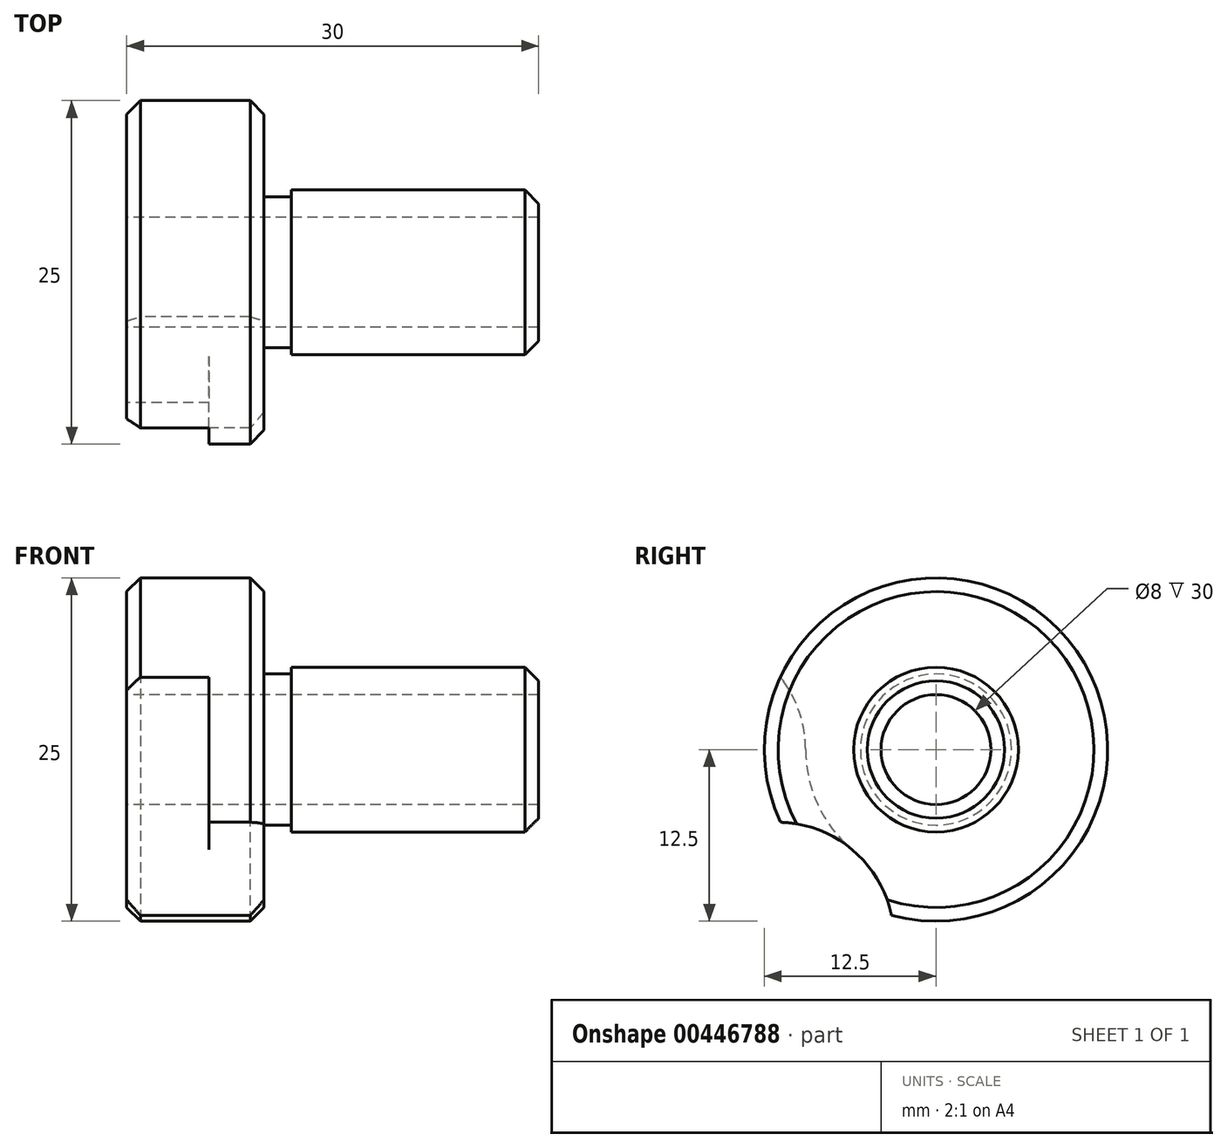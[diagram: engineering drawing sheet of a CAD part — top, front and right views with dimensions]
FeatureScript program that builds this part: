
annotation { "Feature Type Name" : "Feature", "Feature Type Description" : "" }
export const myFeature = defineFeature(function(context is Context, id is Id, definition is map)
    precondition{}
    {
        {
            var Q0;
            Q0=qCreatedBy(makeId("Front.planeOp"),FACE);
            var sketch = newSketch(context, id + "F0", { "sketchPlane" : qUnion([Q0])});
            skLineSegment(sketch, "E0", {"start": v(-5.75, 0) * mm, "end": v(21.36, 0) * mm, "construction": true});
            skLineSegment(sketch, "E1", {"start": v(0, 4) * mm, "end": v(0, 12.5) * mm});
            skLineSegment(sketch, "E2", {"start": v(0, 12.5) * mm, "end": v(10, 12.5) * mm});
            skLineSegment(sketch, "E3", {"start": v(10, 12.5) * mm, "end": v(10, 5.5) * mm});
            skLineSegment(sketch, "E4", {"start": v(10, 5.5) * mm, "end": v(12, 5.5) * mm});
            skLineSegment(sketch, "E5", {"start": v(12, 5.5) * mm, "end": v(12, 6) * mm});
            skLineSegment(sketch, "E6", {"start": v(12, 6) * mm, "end": v(30, 6) * mm});
            skLineSegment(sketch, "E7", {"start": v(30, 6) * mm, "end": v(30, 4) * mm});
            skLineSegment(sketch, "E8", {"start": v(30, 4) * mm, "end": v(0, 4) * mm});
            skSolve(sketch);
        }
        {
            var Q0;
            Q0 = qSketchRegion(id + "F0", true);
            var Q1;
            Q1=sQuery(id+"F0.wireOp",EDGE,"E0");
            revolve(context, id + "F1", {"entities" : qUnion([Q0]), "axis" : qUnion([Q1]), "revolveType" : RevolveType.FULL});
        }
        {
            var Q0;
            Q0=makeQuery(id+"F1.opRevolve","SWEPT_EDGE",EDGE,{"disambiguationData":[OSD([sQuery(id+"F0.wireOp",EDGE,"E6"),sQuery(id+"F0.wireOp",EDGE,"E7")])]});
            var Q1;
            Q1=makeQuery(id+"F1.opRevolve","SWEPT_EDGE",EDGE,{"disambiguationData":[OSD([sQuery(id+"F0.wireOp",EDGE,"E2"),sQuery(id+"F0.wireOp",EDGE,"E3")])]});
            var Q2;
            Q2=makeQuery(id+"F1.opRevolve","SWEPT_EDGE",EDGE,{"disambiguationData":[OSD([sQuery(id+"F0.wireOp",EDGE,"E1"),sQuery(id+"F0.wireOp",EDGE,"E2")])]});
            chamfer(context, id + "F2", {"entities" : qUnion([Q0, Q1, Q2]), "width" : 1 * mm, "tangentPropagation" : true});
        }
        {
            var Q0;
            Q0=makeQuery(id+"F1.opRevolve","SWEPT_FACE",FACE,{"disambiguationData":[OSD([sQuery(id+"F0.wireOp",EDGE,"E1")])]});
            var sketch = newSketch(context, id + "F3", { "sketchPlane" : qUnion([Q0])});
            skLineSegment(sketch, "E9", {"start": v(0, 0) * mm, "end": v(17.54, 0) * mm, "construction": true});
            skLineSegment(sketch, "E10", {"start": v(0, 0) * mm, "end": v(14.34, -17.1) * mm, "construction": true});
            skArc(sketch, "E11", {"start": v(11.32, -5.3) * mm, "mid": v(6.1, -7.28) * mm, "end": v(3.25, -12.07) * mm});
            skArc(sketch, "E12.0", {"start": v(3.25, -12.07) * mm, "mid": v(8.03, -9.58) * mm, "end": v(11.32, -5.3) * mm});
            skSolve(sketch);
        }
        {
            var Q0;
            Q0 = qSketchRegion(id + "F3", true);
            extrude(context, id + "F4", {"entities" : qUnion([Q0]), "operationType" : NewBodyOperationType.REMOVE, "oppositeDirection" : true, "depth" : 10 * mm});
        }
        {
            var Q0;
            Q0=makeQuery(id+"F1.opRevolve","SWEPT_FACE",FACE,{"disambiguationData":[OSD([sQuery(id+"F0.wireOp",EDGE,"E1")])]});
            var sketch = newSketch(context, id + "F5", { "sketchPlane" : qUnion([Q0])});
            skArc(sketch, "E13", {"start": v(6.1, -7.28) * mm, "mid": v(8.6, -4.01) * mm, "end": v(9.5, 0) * mm});
            skArc(sketch, "E14", {"start": v(11.33, 5.27) * mm, "mid": v(9.97, 2.8) * mm, "end": v(9.5, 0) * mm});
            skArc(sketch, "E15.0", {"start": v(11.33, 5.27) * mm, "mid": v(12.5, -0.01) * mm, "end": v(11.32, -5.3) * mm});
            skArc(sketch, "E16.0", {"start": v(10.15, -5.4) * mm, "mid": v(8, -6.07) * mm, "end": v(6.1, -7.28) * mm});
            skArc(sketch, "E17.0", {"start": v(11.32, -5.3) * mm, "mid": v(10.73, -5.33) * mm, "end": v(10.15, -5.4) * mm});
            skPoint(sketch, "E18.orphan", {"position": v(3.25, -12.07) * mm});
            skPoint(sketch, "E19.orphan", {"position": v(3.56, -10.93) * mm});
            skSolve(sketch);
        }
        {
            var Q0;
            Q0 = qSketchRegion(id + "F5", true);
            extrude(context, id + "F6", {"entities" : qUnion([Q0]), "operationType" : NewBodyOperationType.REMOVE, "oppositeDirection" : true, "depth" : 6 * mm});
        }
    });
